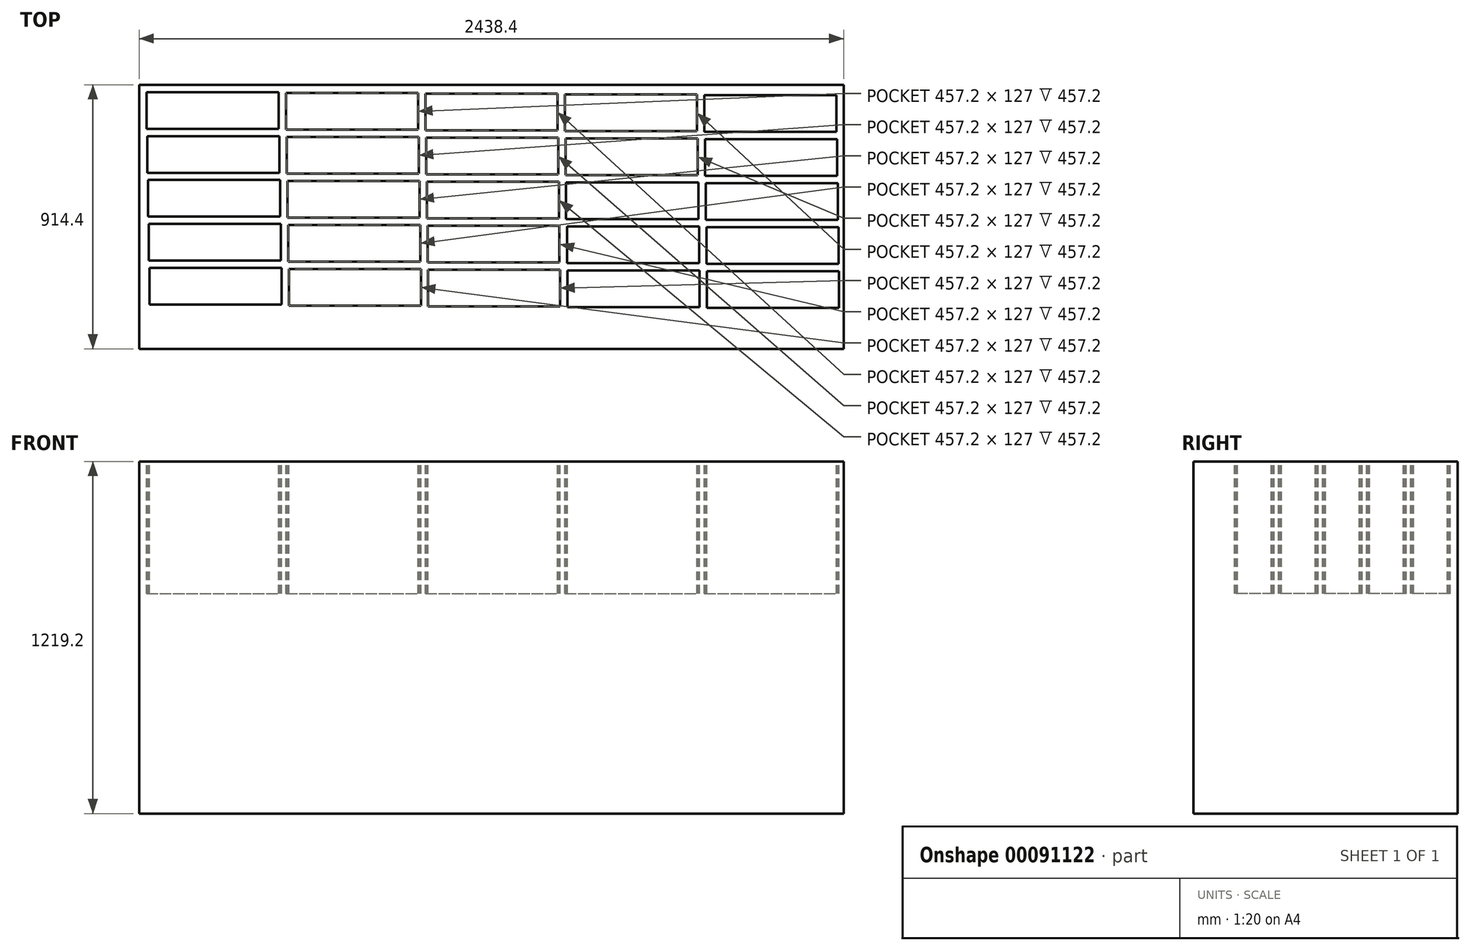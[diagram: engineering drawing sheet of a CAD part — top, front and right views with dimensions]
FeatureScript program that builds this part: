
annotation { "Feature Type Name" : "Feature", "Feature Type Description" : "" }
export const myFeature = defineFeature(function(context is Context, id is Id, definition is map)
    precondition{}
    {
        {
            var Q0;
            Q0=qCreatedBy(makeId("Front.planeOp"),FACE);
            var sketch = newSketch(context, id + "F0", { "sketchPlane" : qUnion([Q0])});
            skLineSegment(sketch, "E0.bottom", {"start": v(-1219.2, 609.6) * mm, "end": v(1219.2, 609.6) * mm});
            skLineSegment(sketch, "E0.top", {"start": v(-1219.2, -609.6) * mm, "end": v(1219.2, -609.6) * mm});
            skLineSegment(sketch, "E0.left", {"start": v(-1219.2, 609.6) * mm, "end": v(-1219.2, -609.6) * mm});
            skLineSegment(sketch, "E0.right", {"start": v(1219.2, 609.6) * mm, "end": v(1219.2, -609.6) * mm});
            skSolve(sketch);
        }
        {
            var Q0;
            Q0 = qSketchRegion(id + "F0", true);
            extrude(context, id + "F1", {"entities" : qUnion([Q0]), "endBound" : BoundingType.SYMMETRIC, "depth" : 914.4 * mm});
        }
        {
            var Q0;
            Q0=makeQuery(id+"F1.opExtrude","SWEPT_FACE",FACE,{"disambiguationData":[OSD([sQuery(id+"F0.wireOp",EDGE,"E0.bottom")])]});
            var sketch = newSketch(context, id + "F2", { "sketchPlane" : qUnion([Q0])});
            skLineSegment(sketch, "E1.bottom", {"start": v(-1193.8, 431.8) * mm, "end": v(-736.6, 431.8) * mm});
            skLineSegment(sketch, "E1.top", {"start": v(-1193.8, 304.8) * mm, "end": v(-736.6, 304.8) * mm});
            skLineSegment(sketch, "E1.left", {"start": v(-1193.8, 431.8) * mm, "end": v(-1193.8, 304.8) * mm});
            skLineSegment(sketch, "E1.right", {"start": v(-736.6, 431.8) * mm, "end": v(-736.6, 304.8) * mm});
            skLineSegment(sketch, "E2.0.1.0", {"start": v(-1191.3, 279.42) * mm, "end": v(-1191.3, 152.42) * mm});
            skLineSegment(sketch, "E2.0.1.1", {"start": v(-1191.3, 152.42) * mm, "end": v(-734.1, 152.42) * mm});
            skLineSegment(sketch, "E2.0.1.2", {"start": v(-734.1, 279.42) * mm, "end": v(-734.1, 152.42) * mm});
            skLineSegment(sketch, "E2.0.1.3", {"start": v(-1191.3, 279.42) * mm, "end": v(-734.1, 279.42) * mm});
            skLineSegment(sketch, "E2.0.2.0", {"start": v(-1188.8, 127.04) * mm, "end": v(-1188.8, 0.04) * mm});
            skLineSegment(sketch, "E2.0.2.1", {"start": v(-1188.8, 0.04) * mm, "end": v(-731.6, 0.04) * mm});
            skLineSegment(sketch, "E2.0.2.2", {"start": v(-731.6, 127.04) * mm, "end": v(-731.6, 0.04) * mm});
            skLineSegment(sketch, "E2.0.2.3", {"start": v(-1188.8, 127.04) * mm, "end": v(-731.6, 127.04) * mm});
            skLineSegment(sketch, "E2.0.3.0", {"start": v(-1186.3, -25.34) * mm, "end": v(-1186.3, -152.34) * mm});
            skLineSegment(sketch, "E2.0.3.1", {"start": v(-1186.3, -152.34) * mm, "end": v(-729.1, -152.34) * mm});
            skLineSegment(sketch, "E2.0.3.2", {"start": v(-729.1, -25.34) * mm, "end": v(-729.1, -152.34) * mm});
            skLineSegment(sketch, "E2.0.3.3", {"start": v(-1186.3, -25.34) * mm, "end": v(-729.1, -25.34) * mm});
            skLineSegment(sketch, "E2.0.4.0", {"start": v(-1183.8, -177.72) * mm, "end": v(-1183.8, -304.72) * mm});
            skLineSegment(sketch, "E2.0.4.1", {"start": v(-1183.8, -304.72) * mm, "end": v(-726.6, -304.72) * mm});
            skLineSegment(sketch, "E2.0.4.2", {"start": v(-726.6, -177.72) * mm, "end": v(-726.6, -304.72) * mm});
            skLineSegment(sketch, "E2.0.4.3", {"start": v(-1183.8, -177.72) * mm, "end": v(-726.6, -177.72) * mm});
            skLineSegment(sketch, "E2.1.0.0", {"start": v(-711.2, 429.04) * mm, "end": v(-711.2, 302.04) * mm});
            skLineSegment(sketch, "E2.1.0.1", {"start": v(-711.2, 302.04) * mm, "end": v(-254, 302.04) * mm});
            skLineSegment(sketch, "E2.1.0.2", {"start": v(-254, 429.04) * mm, "end": v(-254, 302.04) * mm});
            skLineSegment(sketch, "E2.1.0.3", {"start": v(-711.2, 429.04) * mm, "end": v(-254, 429.04) * mm});
            skLineSegment(sketch, "E2.1.1.0", {"start": v(-708.7, 276.66) * mm, "end": v(-708.7, 149.66) * mm});
            skLineSegment(sketch, "E2.1.1.1", {"start": v(-708.7, 149.66) * mm, "end": v(-251.5, 149.66) * mm});
            skLineSegment(sketch, "E2.1.1.2", {"start": v(-251.5, 276.66) * mm, "end": v(-251.5, 149.66) * mm});
            skLineSegment(sketch, "E2.1.1.3", {"start": v(-708.7, 276.66) * mm, "end": v(-251.5, 276.66) * mm});
            skLineSegment(sketch, "E2.1.2.0", {"start": v(-706.2, 124.28) * mm, "end": v(-706.2, -2.72) * mm});
            skLineSegment(sketch, "E2.1.2.1", {"start": v(-706.2, -2.72) * mm, "end": v(-249, -2.72) * mm});
            skLineSegment(sketch, "E2.1.2.2", {"start": v(-249, 124.28) * mm, "end": v(-249, -2.72) * mm});
            skLineSegment(sketch, "E2.1.2.3", {"start": v(-706.2, 124.28) * mm, "end": v(-249, 124.28) * mm});
            skLineSegment(sketch, "E2.1.3.0", {"start": v(-703.7, -28.1) * mm, "end": v(-703.7, -155.1) * mm});
            skLineSegment(sketch, "E2.1.3.1", {"start": v(-703.7, -155.1) * mm, "end": v(-246.5, -155.1) * mm});
            skLineSegment(sketch, "E2.1.3.2", {"start": v(-246.5, -28.1) * mm, "end": v(-246.5, -155.1) * mm});
            skLineSegment(sketch, "E2.1.3.3", {"start": v(-703.7, -28.1) * mm, "end": v(-246.5, -28.1) * mm});
            skLineSegment(sketch, "E2.1.4.0", {"start": v(-701.2, -180.48) * mm, "end": v(-701.2, -307.48) * mm});
            skLineSegment(sketch, "E2.1.4.1", {"start": v(-701.2, -307.48) * mm, "end": v(-244, -307.48) * mm});
            skLineSegment(sketch, "E2.1.4.2", {"start": v(-244, -180.48) * mm, "end": v(-244, -307.48) * mm});
            skLineSegment(sketch, "E2.1.4.3", {"start": v(-701.2, -180.48) * mm, "end": v(-244, -180.48) * mm});
            skLineSegment(sketch, "E2.2.0.0", {"start": v(-228.62, 426.28) * mm, "end": v(-228.62, 299.28) * mm});
            skLineSegment(sketch, "E2.2.0.1", {"start": v(-228.62, 299.28) * mm, "end": v(228.58, 299.28) * mm});
            skLineSegment(sketch, "E2.2.0.2", {"start": v(228.58, 426.28) * mm, "end": v(228.58, 299.28) * mm});
            skLineSegment(sketch, "E2.2.0.3", {"start": v(-228.62, 426.28) * mm, "end": v(228.58, 426.28) * mm});
            skLineSegment(sketch, "E2.2.1.0", {"start": v(-226.11, 273.9) * mm, "end": v(-226.11, 146.9) * mm});
            skLineSegment(sketch, "E2.2.1.1", {"start": v(-226.11, 146.9) * mm, "end": v(231.09, 146.9) * mm});
            skLineSegment(sketch, "E2.2.1.2", {"start": v(231.09, 273.9) * mm, "end": v(231.09, 146.9) * mm});
            skLineSegment(sketch, "E2.2.1.3", {"start": v(-226.11, 273.9) * mm, "end": v(231.09, 273.9) * mm});
            skLineSegment(sketch, "E2.2.2.0", {"start": v(-223.61, 121.53) * mm, "end": v(-223.61, -5.47) * mm});
            skLineSegment(sketch, "E2.2.2.1", {"start": v(-223.61, -5.47) * mm, "end": v(233.59, -5.47) * mm});
            skLineSegment(sketch, "E2.2.2.2", {"start": v(233.59, 121.53) * mm, "end": v(233.59, -5.47) * mm});
            skLineSegment(sketch, "E2.2.2.3", {"start": v(-223.61, 121.53) * mm, "end": v(233.59, 121.53) * mm});
            skLineSegment(sketch, "E2.2.3.0", {"start": v(-221.1, -30.85) * mm, "end": v(-221.1, -157.85) * mm});
            skLineSegment(sketch, "E2.2.3.1", {"start": v(-221.1, -157.85) * mm, "end": v(236.1, -157.85) * mm});
            skLineSegment(sketch, "E2.2.3.2", {"start": v(236.1, -30.85) * mm, "end": v(236.1, -157.85) * mm});
            skLineSegment(sketch, "E2.2.3.3", {"start": v(-221.1, -30.85) * mm, "end": v(236.1, -30.85) * mm});
            skLineSegment(sketch, "E2.2.4.0", {"start": v(-218.6, -183.23) * mm, "end": v(-218.6, -310.23) * mm});
            skLineSegment(sketch, "E2.2.4.1", {"start": v(-218.6, -310.23) * mm, "end": v(238.6, -310.23) * mm});
            skLineSegment(sketch, "E2.2.4.2", {"start": v(238.6, -183.23) * mm, "end": v(238.6, -310.23) * mm});
            skLineSegment(sketch, "E2.2.4.3", {"start": v(-218.6, -183.23) * mm, "end": v(238.6, -183.23) * mm});
            skLineSegment(sketch, "E2.3.0.0", {"start": v(253.98, 423.53) * mm, "end": v(253.98, 296.53) * mm});
            skLineSegment(sketch, "E2.3.0.1", {"start": v(253.98, 296.53) * mm, "end": v(711.18, 296.53) * mm});
            skLineSegment(sketch, "E2.3.0.2", {"start": v(711.18, 423.53) * mm, "end": v(711.18, 296.53) * mm});
            skLineSegment(sketch, "E2.3.0.3", {"start": v(253.98, 423.53) * mm, "end": v(711.18, 423.53) * mm});
            skLineSegment(sketch, "E2.3.1.0", {"start": v(256.48, 271.15) * mm, "end": v(256.48, 144.15) * mm});
            skLineSegment(sketch, "E2.3.1.1", {"start": v(256.48, 144.15) * mm, "end": v(713.68, 144.15) * mm});
            skLineSegment(sketch, "E2.3.1.2", {"start": v(713.68, 271.15) * mm, "end": v(713.68, 144.15) * mm});
            skLineSegment(sketch, "E2.3.1.3", {"start": v(256.48, 271.15) * mm, "end": v(713.68, 271.15) * mm});
            skLineSegment(sketch, "E2.3.2.0", {"start": v(258.98, 118.77) * mm, "end": v(258.98, -8.23) * mm});
            skLineSegment(sketch, "E2.3.2.1", {"start": v(258.98, -8.23) * mm, "end": v(716.18, -8.23) * mm});
            skLineSegment(sketch, "E2.3.2.2", {"start": v(716.18, 118.77) * mm, "end": v(716.18, -8.23) * mm});
            skLineSegment(sketch, "E2.3.2.3", {"start": v(258.98, 118.77) * mm, "end": v(716.18, 118.77) * mm});
            skLineSegment(sketch, "E2.3.3.0", {"start": v(261.48, -33.61) * mm, "end": v(261.48, -160.61) * mm});
            skLineSegment(sketch, "E2.3.3.1", {"start": v(261.48, -160.61) * mm, "end": v(718.68, -160.61) * mm});
            skLineSegment(sketch, "E2.3.3.2", {"start": v(718.68, -33.61) * mm, "end": v(718.68, -160.61) * mm});
            skLineSegment(sketch, "E2.3.3.3", {"start": v(261.48, -33.61) * mm, "end": v(718.68, -33.61) * mm});
            skLineSegment(sketch, "E2.3.4.0", {"start": v(263.99, -186) * mm, "end": v(263.99, -313) * mm});
            skLineSegment(sketch, "E2.3.4.1", {"start": v(263.99, -313) * mm, "end": v(721.19, -313) * mm});
            skLineSegment(sketch, "E2.3.4.2", {"start": v(721.19, -186) * mm, "end": v(721.19, -313) * mm});
            skLineSegment(sketch, "E2.3.4.3", {"start": v(263.99, -186) * mm, "end": v(721.19, -186) * mm});
            skLineSegment(sketch, "E2.4.0.0", {"start": v(736.57, 420.77) * mm, "end": v(736.57, 293.77) * mm});
            skLineSegment(sketch, "E2.4.0.1", {"start": v(736.57, 293.77) * mm, "end": v(1193.77, 293.77) * mm});
            skLineSegment(sketch, "E2.4.0.2", {"start": v(1193.77, 420.77) * mm, "end": v(1193.77, 293.77) * mm});
            skLineSegment(sketch, "E2.4.0.3", {"start": v(736.57, 420.77) * mm, "end": v(1193.77, 420.77) * mm});
            skLineSegment(sketch, "E2.4.1.0", {"start": v(739.07, 268.39) * mm, "end": v(739.07, 141.39) * mm});
            skLineSegment(sketch, "E2.4.1.1", {"start": v(739.07, 141.39) * mm, "end": v(1196.27, 141.39) * mm});
            skLineSegment(sketch, "E2.4.1.2", {"start": v(1196.27, 268.39) * mm, "end": v(1196.27, 141.39) * mm});
            skLineSegment(sketch, "E2.4.1.3", {"start": v(739.07, 268.39) * mm, "end": v(1196.27, 268.39) * mm});
            skLineSegment(sketch, "E2.4.2.0", {"start": v(741.57, 116) * mm, "end": v(741.57, -11) * mm});
            skLineSegment(sketch, "E2.4.2.1", {"start": v(741.57, -11) * mm, "end": v(1198.77, -11) * mm});
            skLineSegment(sketch, "E2.4.2.2", {"start": v(1198.77, 116) * mm, "end": v(1198.77, -11) * mm});
            skLineSegment(sketch, "E2.4.2.3", {"start": v(741.57, 116) * mm, "end": v(1198.77, 116) * mm});
            skLineSegment(sketch, "E2.4.3.0", {"start": v(744.08, -36.37) * mm, "end": v(744.08, -163.37) * mm});
            skLineSegment(sketch, "E2.4.3.1", {"start": v(744.08, -163.37) * mm, "end": v(1201.28, -163.37) * mm});
            skLineSegment(sketch, "E2.4.3.2", {"start": v(1201.28, -36.37) * mm, "end": v(1201.28, -163.37) * mm});
            skLineSegment(sketch, "E2.4.3.3", {"start": v(744.08, -36.37) * mm, "end": v(1201.28, -36.37) * mm});
            skLineSegment(sketch, "E2.4.4.0", {"start": v(746.58, -188.75) * mm, "end": v(746.58, -315.75) * mm});
            skLineSegment(sketch, "E2.4.4.1", {"start": v(746.58, -315.75) * mm, "end": v(1203.78, -315.75) * mm});
            skLineSegment(sketch, "E2.4.4.2", {"start": v(1203.78, -188.75) * mm, "end": v(1203.78, -315.75) * mm});
            skLineSegment(sketch, "E2.4.4.3", {"start": v(746.58, -188.75) * mm, "end": v(1203.78, -188.75) * mm});
            skLineSegment(sketch, "E2.direction1", {"start": v(-1193.8, 304.8) * mm, "end": v(-711.2, 302.04) * mm, "construction": true});
            skLineSegment(sketch, "E2.direction2", {"start": v(-1193.8, 304.8) * mm, "end": v(-1191.3, 152.42) * mm, "construction": true});
            skSolve(sketch);
        }
        {
            var Q0;
            Q0 = qSketchRegion(id + "F2", true);
            extrude(context, id + "F3", {"entities" : qUnion([Q0]), "operationType" : NewBodyOperationType.REMOVE, "oppositeDirection" : true, "depth" : 457.2 * mm});
        }
    });
